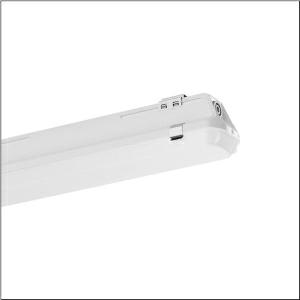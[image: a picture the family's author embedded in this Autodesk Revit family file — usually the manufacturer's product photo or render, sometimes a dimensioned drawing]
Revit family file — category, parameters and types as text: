
# Revit family: monsun_r__11_facade_51ff40mp360h_5056
name_source: partatom
category: Lighting Fixtures
units: mm (PartAtom-declared; Revit-internal decimal feet)

## family parameters
Cut with Voids When Loaded = No
Host = Face
Light Source = No
Part Type = Normal
Room Calculation Point = No
Round Connector Dimension = Use Diameter
Shared = No

## types (1)
- --- (1 x LED, 5790 lm, 33.6 W, 3000K)
    Apparent Load = 34 VA
    CIE Flux Codes = 47 77 93 95 100
    Color Rendering = 80
    Color Temperature = 3000K
    Default Elevation = 1800 mm
    Description = Monsun® 11 facade, damp-proof luminaire, chain hanger, primary optical cover: enclosure, of PMMA, light emission: direct distribution, primary light characteristic: symmetric, installation type: vertical mounting, horizontal mounting, surface-mounted, LED, rated luminous flux: 5.790lm, luminous efficacy: 172lm/W, light colour: 830, colour temperature: 3000K, control gear: ECG, with terminal, 3-pole, max. 2.5mm², mains connection: 220..240V, AC, 50/60Hz, rated input power: 34W, luminaire housing, of glass-fibre reinforced polyester, uncoated, bright grey, with climate membrane, for cables, Ø 8.4..12mm, incl. chain hanger, length: 1.590mm, width: 90mm, height: 88mm, clip for enclosure, of stainless steel (V2A), ceiling mounting element, of stainless steel (V2A), chain hanger, of stainless steel (V2A), protection rating (complete): IP66, insulation class (complete): insulation class I (protective earthing), certification: CE, ENEC, VDE, UKCA, protection symbol: D, impact resistance: IK06, permissible operating ambient temperature: -35..+50°C, standard: EN 60598-2-1, EN 50419, exposed outdoor area, contact your sales advisor before using the luminaires in applications with unclear chemical exposure, large temperature fluctuations or condensation-forming humidity, LABS conformity tested according to VDMA 24364:2018-05, packaging unit: 1 piece
    Height = 89 mm
    Lamp = 1 x LED
    Lamp Light Flux = 5790 lm
    Lamp Power = 33.6 W
    Lamp count = 1
    Length = 1590 mm
    Luminous efficacy = 172 lm/W
    Manufacturer = Siteco
    ModVariant = No
    Model = 51FF40MP360H
    Mounting Place = Ceiling
    Mounting Type = Surface mounted
    Number of Poles = 1
    OnlyDefault = Yes
    Power Factor = 1
    Product Name = Monsun® 11 facade
    Product group = damp-proof luminaire
    ProductGroupID = 300
    Protection Class = Protection class I
    Protection Degree = IP 66
    RLX_Detail_Level = 1
    RLX_Emergency_Light_Flux = 0 lm
    RLX_Emergency_Type = 0
    RLX_Emergency_Type_DB = No
    RlxData = <blob elided: 89653 chars, md5=482c18de>
    Socket = socket
    Standby Power = 0 W
    System Light Flux = 5790 lm
    System Power = 34 W
    Type Comments = factory setting: luminous flux: 100 % | (A | C | E) | 77 mA
    Type Image = l_1319650.jpg
    URL = http://relux.com
    VarID = @adj_113141
    Voltage = 0 V
    Weight = 0.00 kg
    Width = 90 mm

## geometry (parser evidence)
native form markers: Blend x4, Sweep x12
no freeform markers — native parametric forms only
